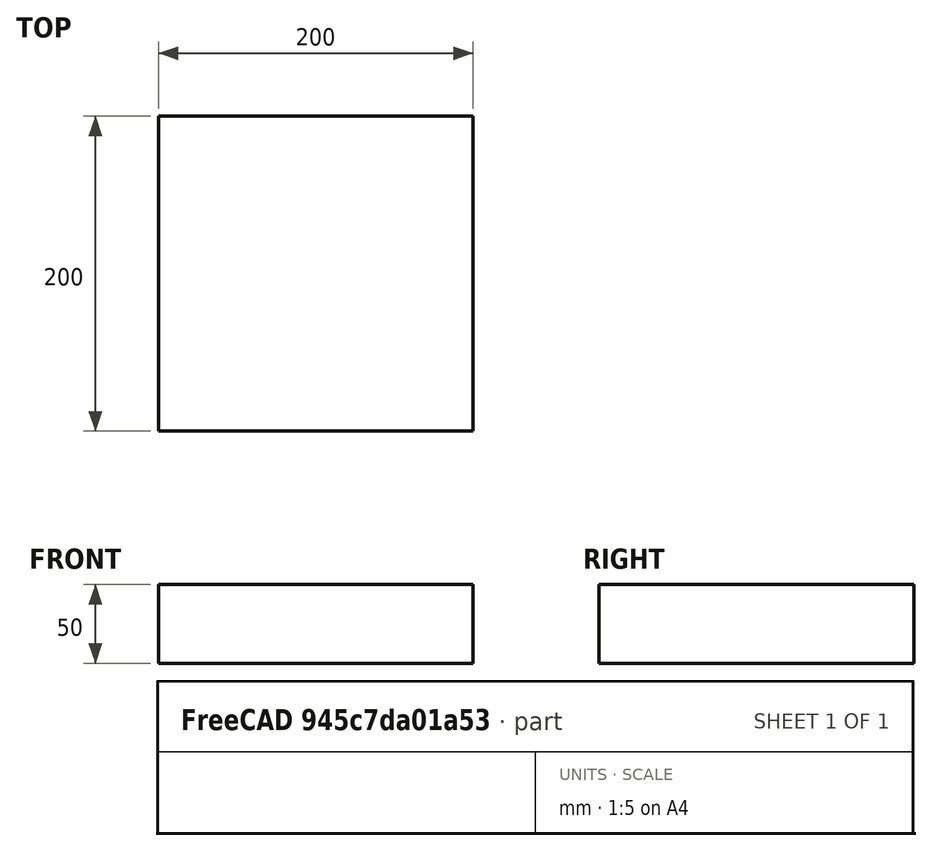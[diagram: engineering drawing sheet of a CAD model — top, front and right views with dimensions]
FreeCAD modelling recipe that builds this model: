
FCSTD DOCUMENT  (FreeCAD 0.15R4671 (Git))
Label: Square Bar 200 EN10059 S235JR
License: All rights reserved
LicenseURL: http://en.wikipedia.org/wiki/All_rights_reserved
objects: Sketcher::SketchObject×1, Part::Extrusion×1
note: 2 computed .brp shape members not serialized (recipe doc carries the construction recipe); baked Part::Feature solids carry a one-line shape summary decoded from their .brp

FEATURE [Sketcher::SketchObject] Sketch
  sketch-geometry (4):
    g0: LineSegment StartX=-100 StartY=-100 StartZ=0 EndX=100 EndY=-100 EndZ=0
    g1: LineSegment StartX=100 StartY=-100 StartZ=0 EndX=100 EndY=100 EndZ=0
    g2: LineSegment StartX=100 StartY=100 StartZ=0 EndX=-100 EndY=100 EndZ=0
    g3: LineSegment StartX=-100 StartY=100 StartZ=0 EndX=-100 EndY=-100 EndZ=0
  constraints (12):
    c: Coincident(g0,g1)
    c: Coincident(g1,g2)
    c: Coincident(g2,g3)
    c: Coincident(g3,g0)
    c: Horizontal(g0)
    c: Horizontal(g2)
    c: Vertical(g1)
    c: Vertical(g3)
    c: Symmetric(g1,g0,g-1)
    c: Symmetric(g2,g1,g-2)
    c: Equal(g1,g2)
    c: DistanceY(g1) = 200
FEATURE [Part::Extrusion] Extrude  label="Square Bar 200 EN10059 S235JR"
  Base = -> Sketch
  Dir = (0,0,50)
  Solid = true
